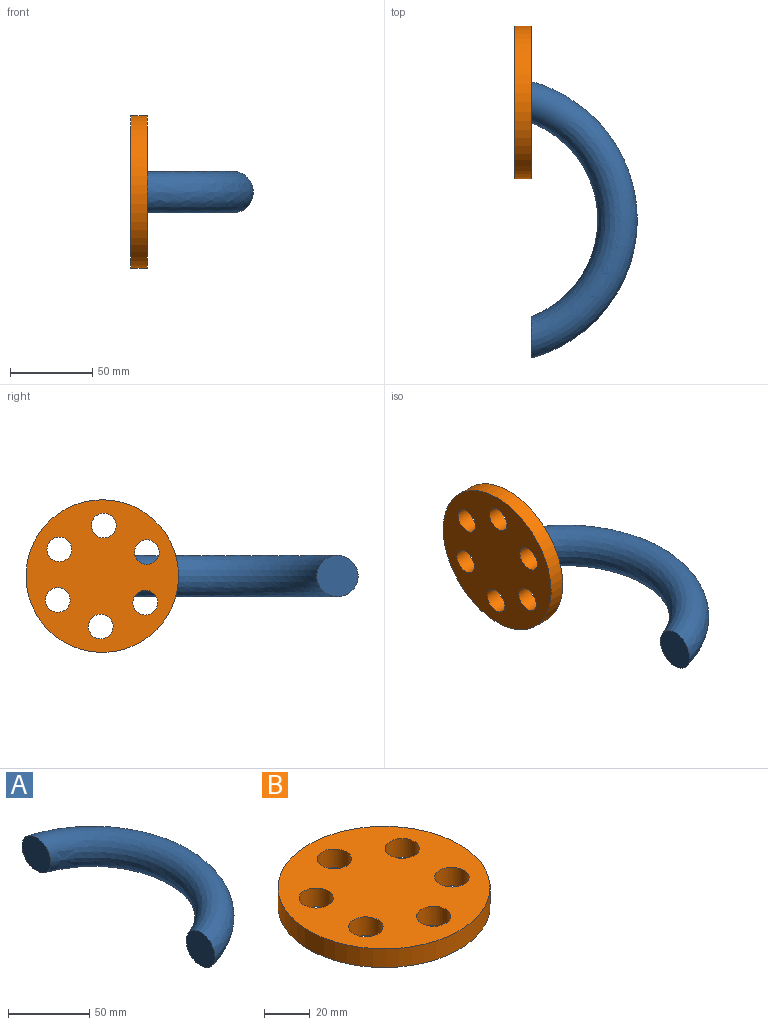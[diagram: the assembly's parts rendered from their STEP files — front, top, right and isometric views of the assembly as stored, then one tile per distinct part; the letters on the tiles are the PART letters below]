
ASSEMBLY  parts=2 mates=1
PART A: 3 faces, bbox 76.9x167.7x25.1 mm
  f0: revolved ~167.66x76.87mm, area 14581.1mm2, adj f1,f2
  f1: plane 25.12x25.11mm, normal (-1,0,0), area 495.1mm2, adj f0
  f2: plane 25.11x25.11mm, normal (-1,0,0), area 495.3mm2, adj f0
PART B: 9 faces, bbox 92.6x92.6x10 mm
  f0: cylinder r=7.49mm len=14.98mm, axis (0,0,-1), area 470.6mm2, adj f7,f8
  f1: cylinder r=7.49mm len=14.98mm, axis (0,0,-1), area 470.6mm2, adj f7,f8
  f2: cylinder r=7.49mm len=14.98mm, axis (0,0,-1), area 470.6mm2, adj f7,f8
  f3: cylinder r=7.49mm len=14.98mm, axis (0,0,-1), area 470.6mm2, adj f7,f8
  f4: cylinder r=7.49mm len=14.98mm, axis (0,0,-1), area 470.6mm2, adj f7,f8
  f5: cylinder r=7.49mm len=14.98mm, axis (0,0,-1), area 470.6mm2, adj f7,f8
  f6: cylinder r=46.28mm len=92.57mm, axis (0,0,-1), area 2908.1mm2, adj f7,f8
  f7: plane 92.57x92.57mm, normal (0,0,1), area 5672.5mm2, adj f0,f1,f2,f3,f4,f5,f6
  f8: plane 92.57x92.57mm, normal (0,0,-1), area 5672.5mm2, adj f0,f1,f2,f3,f4,f5,f6
PLACE A at identity fixed
PLACE B rot(axis=(0.7,0.18,0.7),160.1deg) t=(-10,158.29,-61.76)mm
MATE revolute B.f6 <-> A.f1  axis (1,0,0) through (0,85.77,0)mm
